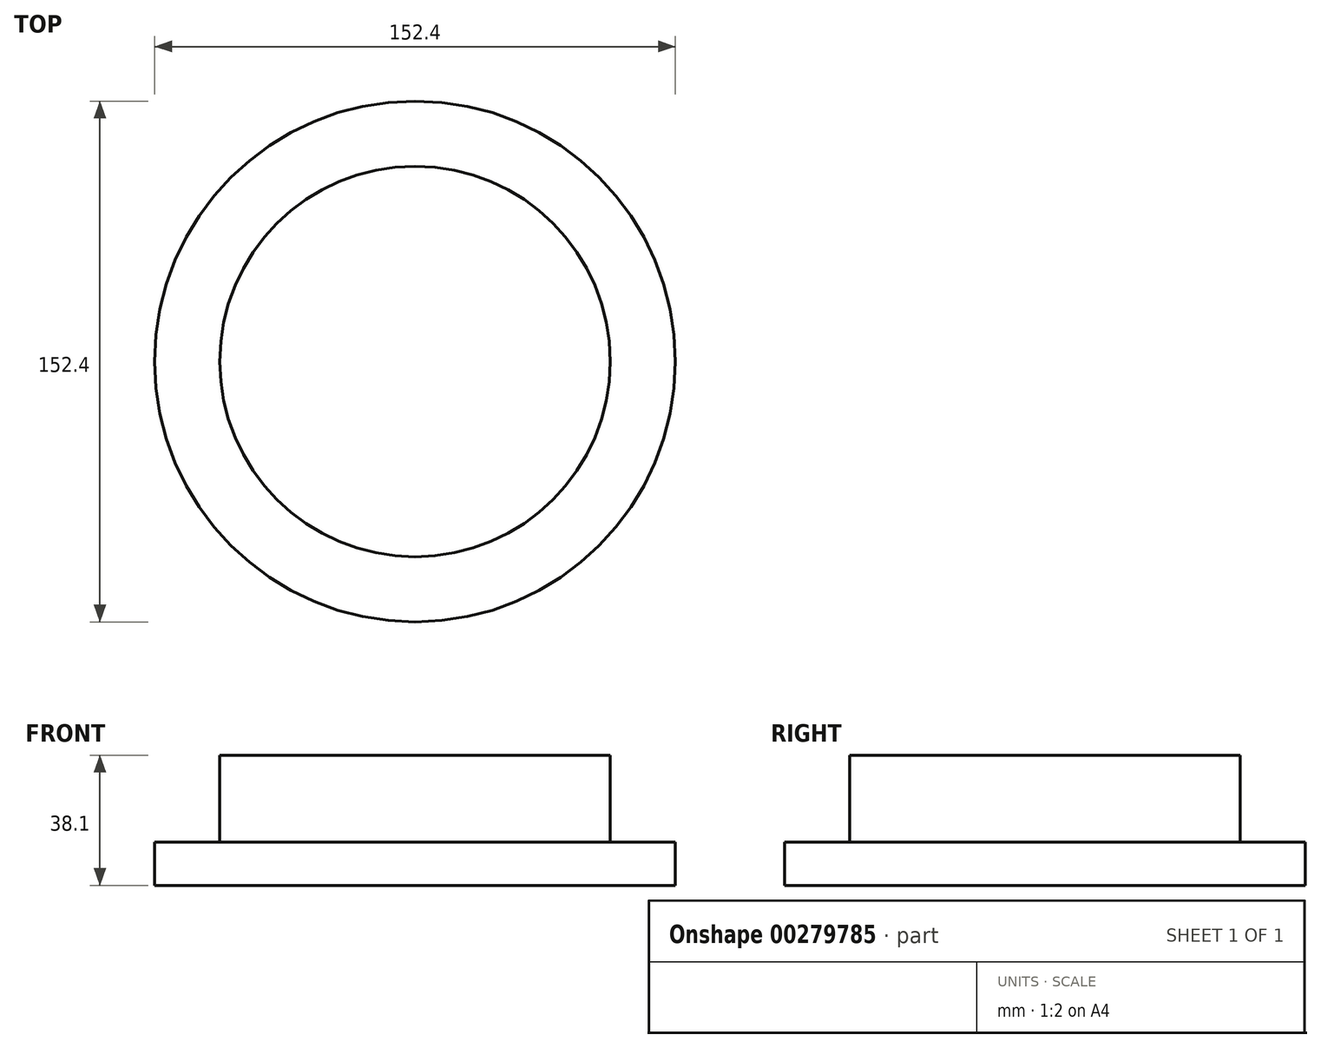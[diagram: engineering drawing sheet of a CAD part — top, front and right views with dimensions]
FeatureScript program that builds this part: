
annotation { "Feature Type Name" : "Feature", "Feature Type Description" : "" }
export const myFeature = defineFeature(function(context is Context, id is Id, definition is map)
    precondition{}
    {
        {
            var Q0;
            Q0=qCreatedBy(makeId("Top.planeOp"),FACE);
            var sketch = newSketch(context, id + "F0", { "sketchPlane" : qUnion([Q0])});
            skCircle(sketch, "E0", {"center": v(0, 0) * mm, "radius": 76.2 * mm});
            skSolve(sketch);
        }
        {
            var Q0;
            Q0 = qSketchRegion(id + "F0", true);
            extrude(context, id + "F1", {"entities" : qUnion([Q0]), "depth" : 12.7 * mm});
        }
        {
            var Q0;
            Q0=qCreatedBy(makeId("Top.planeOp"),FACE);
            var sketch = newSketch(context, id + "F2", { "sketchPlane" : qUnion([Q0])});
            skCircle(sketch, "E1", {"center": v(0, 0) * mm, "radius": 12.7 * mm});
            skSolve(sketch);
        }
        {
            var Q0;
            Q0=sQuery(id+"F2.wireOp",EDGE,"E1");
            extrude(context, id + "F3", {"bodyType" : ToolBodyType.SURFACE, "surfaceEntities" : qUnion([Q0]), "depth" : 76.2 * mm});
        }
        {
            var Q0;
            Q0=qCreatedBy(makeId("Top.planeOp"),FACE);
            var sketch = newSketch(context, id + "F4", { "sketchPlane" : qUnion([Q0])});
            skCircle(sketch, "E2", {"center": v(0, 0) * mm, "radius": 69.85 * mm});
            skSolve(sketch);
        }
        {
            var Q0;
            Q0=sQuery(id+"F4.wireOp",EDGE,"E2");
            extrude(context, id + "F5", {"bodyType" : ToolBodyType.SURFACE, "operationType" : NewBodyOperationType.ADD, "surfaceEntities" : qUnion([Q0]), "depth" : 25.4 * mm});
        }
        {
            var Q0;
            Q0=qCreatedBy(makeId("Top.planeOp"),FACE);
            var sketch = newSketch(context, id + "F6", { "sketchPlane" : qUnion([Q0])});
            skCircle(sketch, "E3", {"center": v(0, 0) * mm, "radius": 57.15 * mm});
            skSolve(sketch);
        }
        {
            var Q0;
            Q0 = qSketchRegion(id + "F6", true);
            extrude(context, id + "F7", {"entities" : qUnion([Q0]), "operationType" : NewBodyOperationType.ADD, "depth" : 38.1 * mm});
        }
        {
            var Q0;
            Q0=qCreatedBy(makeId("Top.planeOp"),FACE);
            var sketch = newSketch(context, id + "F8", { "sketchPlane" : qUnion([Q0])});
            skCircle(sketch, "E4", {"center": v(0, 0) * mm, "radius": 44.45 * mm});
            skSolve(sketch);
        }
        {
            var Q0;
            Q0=sQuery(id+"F8.wireOp",EDGE,"E4");
            extrude(context, id + "F9", {"bodyType" : ToolBodyType.SURFACE, "surfaceEntities" : qUnion([Q0]), "depth" : 50.8 * mm});
        }
    });
